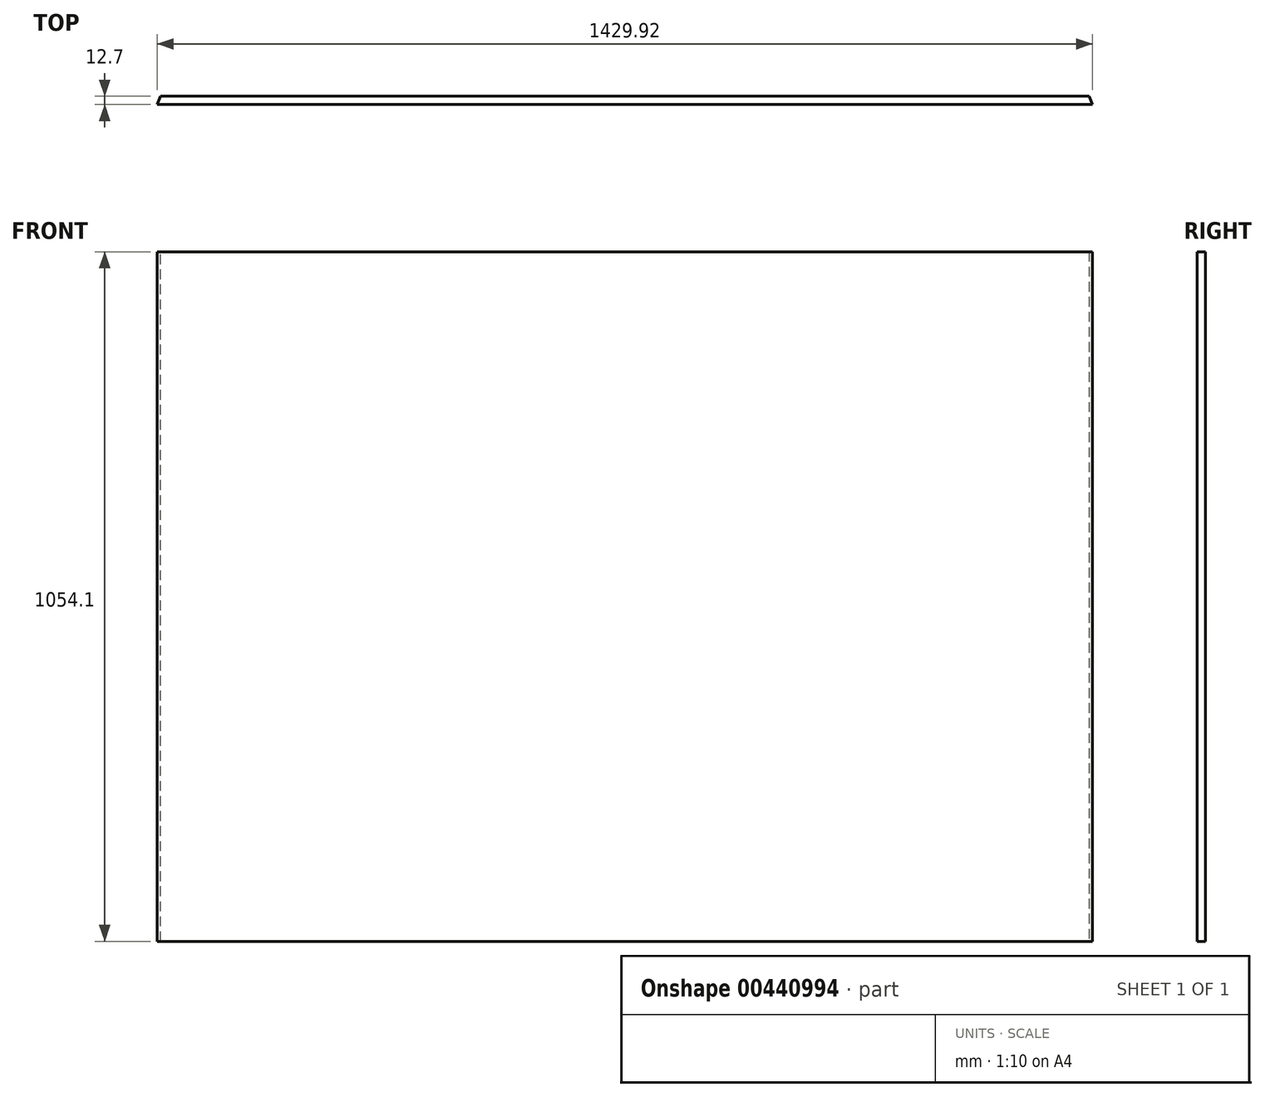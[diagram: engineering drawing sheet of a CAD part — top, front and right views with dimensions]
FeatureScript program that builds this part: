
annotation { "Feature Type Name" : "Feature", "Feature Type Description" : "" }
export const myFeature = defineFeature(function(context is Context, id is Id, definition is map)
    precondition{}
    {
        {
            var Q0;
            Q0=qCreatedBy(makeId("Front.planeOp"),FACE);
            var sketch = newSketch(context, id + "F0", { "sketchPlane" : qUnion([Q0])});
            skLineSegment(sketch, "E0.bottom", {"start": v(0, 0) * mm, "end": v(1429.92, 0) * mm});
            skLineSegment(sketch, "E0.top", {"start": v(0, 1054.1) * mm, "end": v(1429.92, 1054.1) * mm});
            skLineSegment(sketch, "E0.left", {"start": v(0, 0) * mm, "end": v(0, 1054.1) * mm});
            skLineSegment(sketch, "E0.right", {"start": v(1429.92, 0) * mm, "end": v(1429.92, 1054.1) * mm});
            skSolve(sketch);
        }
        {
            var Q0;
            Q0=makeQuery(id+"F0.imprint","IMPRINT",FACE,{"disambiguationData":[TD([[makeQuery(id+"F0.imprint","IMPRINT",EDGE,{"derivedFrom":sQuery(id+"F0.wireOp",EDGE,"E0.bottom")}),1.0]])]});
            extrude(context, id + "F1", {"entities" : qUnion([Q0]), "oppositeDirection" : true, "depth" : 12.7 * mm});
        }
        {
            var Q0;
            Q0=makeQuery(id+"F1.opExtrude","CAP_EDGE",EDGE,{"disambiguationData":[OSD([sQuery(id+"F0.wireOp",EDGE,"E0.right")])],"isStart":false});
            var Q1;
            Q1=makeQuery(id+"F1.opExtrude","CAP_EDGE",EDGE,{"disambiguationData":[OSD([sQuery(id+"F0.wireOp",EDGE,"E0.left")])],"isStart":false});
            chamfer(context, id + "F2", {"entities" : qUnion([Q0, Q1]), "chamferType" : ChamferType.OFFSET_ANGLE, "width" : 12.7 * mm, "oppositeDirection" : false, "angle" : 22.5 * degree, "tangentPropagation" : true});
        }
    });
